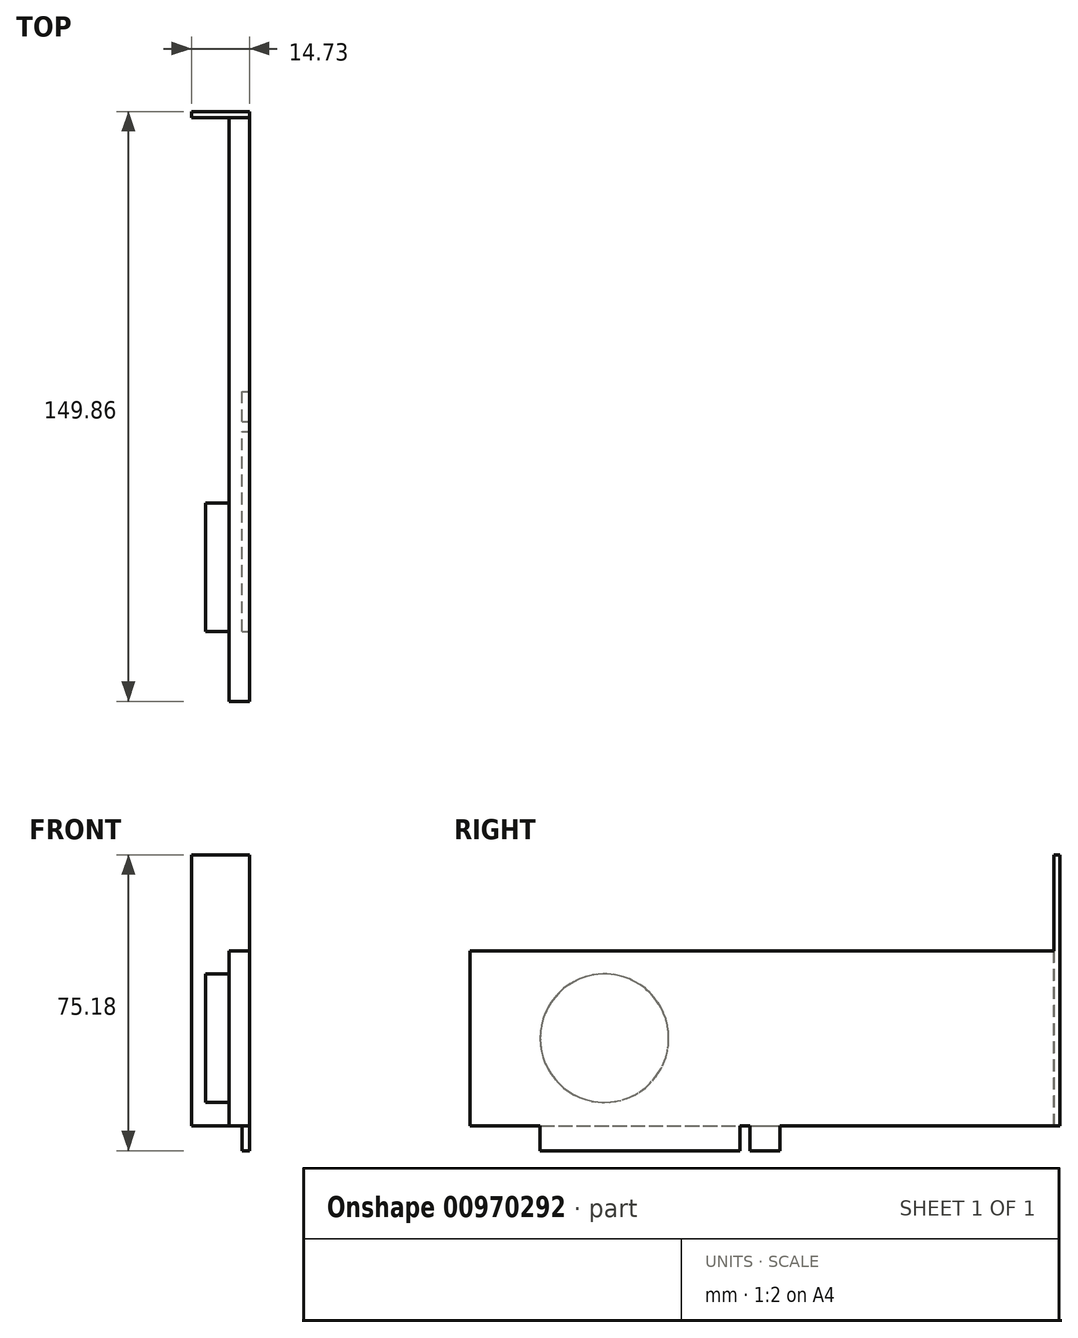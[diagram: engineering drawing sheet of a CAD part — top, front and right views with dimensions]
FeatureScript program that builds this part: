
annotation { "Feature Type Name" : "Feature", "Feature Type Description" : "" }
export const myFeature = defineFeature(function(context is Context, id is Id, definition is map)
    precondition{}
    {
        {
            var Q0;
            Q0=qCreatedBy(makeId("Front.planeOp"),FACE);
            var sketch = newSketch(context, id + "F0", { "sketchPlane" : qUnion([Q0])});
            skLineSegment(sketch, "E0.bottom", {"start": v(0, 0) * mm, "end": v(-14.73, 0) * mm});
            skLineSegment(sketch, "E0.top", {"start": v(0, 68.83) * mm, "end": v(-14.73, 68.83) * mm});
            skLineSegment(sketch, "E0.left", {"start": v(0, 0) * mm, "end": v(0, 68.83) * mm});
            skLineSegment(sketch, "E0.right", {"start": v(-14.73, 0) * mm, "end": v(-14.73, 68.83) * mm});
            skLineSegment(sketch, "E1", {"start": v(-5.08, 44.45) * mm, "end": v(-5.08, 0) * mm});
            skLineSegment(sketch, "E2", {"start": v(-5.08, 44.45) * mm, "end": v(0, 44.45) * mm});
            skSolve(sketch);
        }
        {
            var Q0;
            {var subQ3=sQuery(id+"F0.wireOp",EDGE,"E1");Q0=makeQuery(id+"F0.imprint","IMPRINT",FACE,{"disambiguationData":[TD([[makeQuery(id+"F0.imprint","IMPRINT",EDGE,{"derivedFrom":subQ3}),1.0]])]});}
            extrude(context, id + "F1", {"entities" : qUnion([Q0]), "depth" : 149.86 * mm, "offsetDistance" : 25.4 * mm});
        }
        {
            var Q0;
            {var subQ2=sQuery(id+"F0.wireOp",EDGE,"E0.top");Q0=makeQuery(id+"F0.imprint","IMPRINT",FACE,{"disambiguationData":[TD([[makeQuery(id+"F0.imprint","IMPRINT",EDGE,{"derivedFrom":subQ2}),1.0]])]});}
            extrude(context, id + "F2", {"entities" : qUnion([Q0]), "operationType" : NewBodyOperationType.ADD, "depth" : 1.59 * mm, "offsetDistance" : 25.4 * mm});
        }
        {
            var Q0;
            {var subQ0=sQuery(id+"F0.wireOp",EDGE,"E0.left");Q0=makeQuery(id+"F2.boolean.opBoolean","MERGE",FACE,{"derivedFrom":[makeQuery(id+"F1.opExtrude","SWEPT_FACE",FACE,{"disambiguationData":[OSD([subQ0])]}),makeQuery(id+"F2.opExtrude","SWEPT_FACE",FACE,{"disambiguationData":[OSD([subQ0])]})]});}
            var sketch = newSketch(context, id + "F3", { "sketchPlane" : qUnion([Q0])});
            skLineSegment(sketch, "E3", {"start": v(-132.08, 0) * mm, "end": v(-132.08, -6.35) * mm});
            skLineSegment(sketch, "E4", {"start": v(-132.08, -6.35) * mm, "end": v(-81.28, -6.35) * mm});
            skLineSegment(sketch, "E5", {"start": v(-81.28, -6.35) * mm, "end": v(-81.28, 0) * mm});
            skLineSegment(sketch, "E6", {"start": v(-78.74, 0) * mm, "end": v(-78.74, -6.35) * mm});
            skLineSegment(sketch, "E7", {"start": v(-78.74, -6.35) * mm, "end": v(-71.12, -6.35) * mm});
            skLineSegment(sketch, "E8", {"start": v(-71.12, -6.35) * mm, "end": v(-71.12, 0) * mm});
            skSolve(sketch);
        }
        {
            var Q0;
            {var subQ0=sQuery(id+"F3.wireOp",EDGE,"E6");Q0=makeQuery(id+"F3.imprint","IMPRINT",FACE,{"disambiguationData":[TD([[makeQuery(id+"F3.imprint","IMPRINT",EDGE,{"derivedFrom":subQ0}),1.0]])]});}
            var Q1;
            {var subQ0=sQuery(id+"F3.wireOp",EDGE,"E3");Q1=makeQuery(id+"F3.imprint","IMPRINT",FACE,{"disambiguationData":[TD([[makeQuery(id+"F3.imprint","IMPRINT",EDGE,{"derivedFrom":subQ0}),1.0]])]});}
            extrude(context, id + "F4", {"entities" : qUnion([Q0, Q1]), "operationType" : NewBodyOperationType.ADD, "oppositeDirection" : true, "depth" : 1.78 * mm, "offsetDistance" : 25.4 * mm});
        }
        {
            var Q0;
            Q0=makeQuery(id+"F1.opExtrude","SWEPT_FACE",FACE,{"disambiguationData":[OSD([sQuery(id+"F0.wireOp",EDGE,"E1")])]});
            var sketch = newSketch(context, id + "F5", { "sketchPlane" : qUnion([Q0])});
            skLineSegment(sketch, "E9", {"start": v(149.86, 22.22) * mm, "end": v(92.38, 22.22) * mm, "construction": true});
            skCircle(sketch, "E10", {"center": v(115.76, 22.22) * mm, "radius": 16.32 * mm});
            skSolve(sketch);
        }
        {
            var Q0;
            Q0=makeQuery(id+"F5.imprint","IMPRINT",FACE,{"disambiguationData":[TD([[makeQuery(id+"F5.imprint","IMPRINT",EDGE,{"derivedFrom":sQuery(id+"F5.wireOp",EDGE,"E10")}),1.0]])]});
            extrude(context, id + "F6", {"entities" : qUnion([Q0]), "operationType" : NewBodyOperationType.ADD, "depth" : 6.1 * mm, "offsetDistance" : 25.4 * mm});
        }
    });
